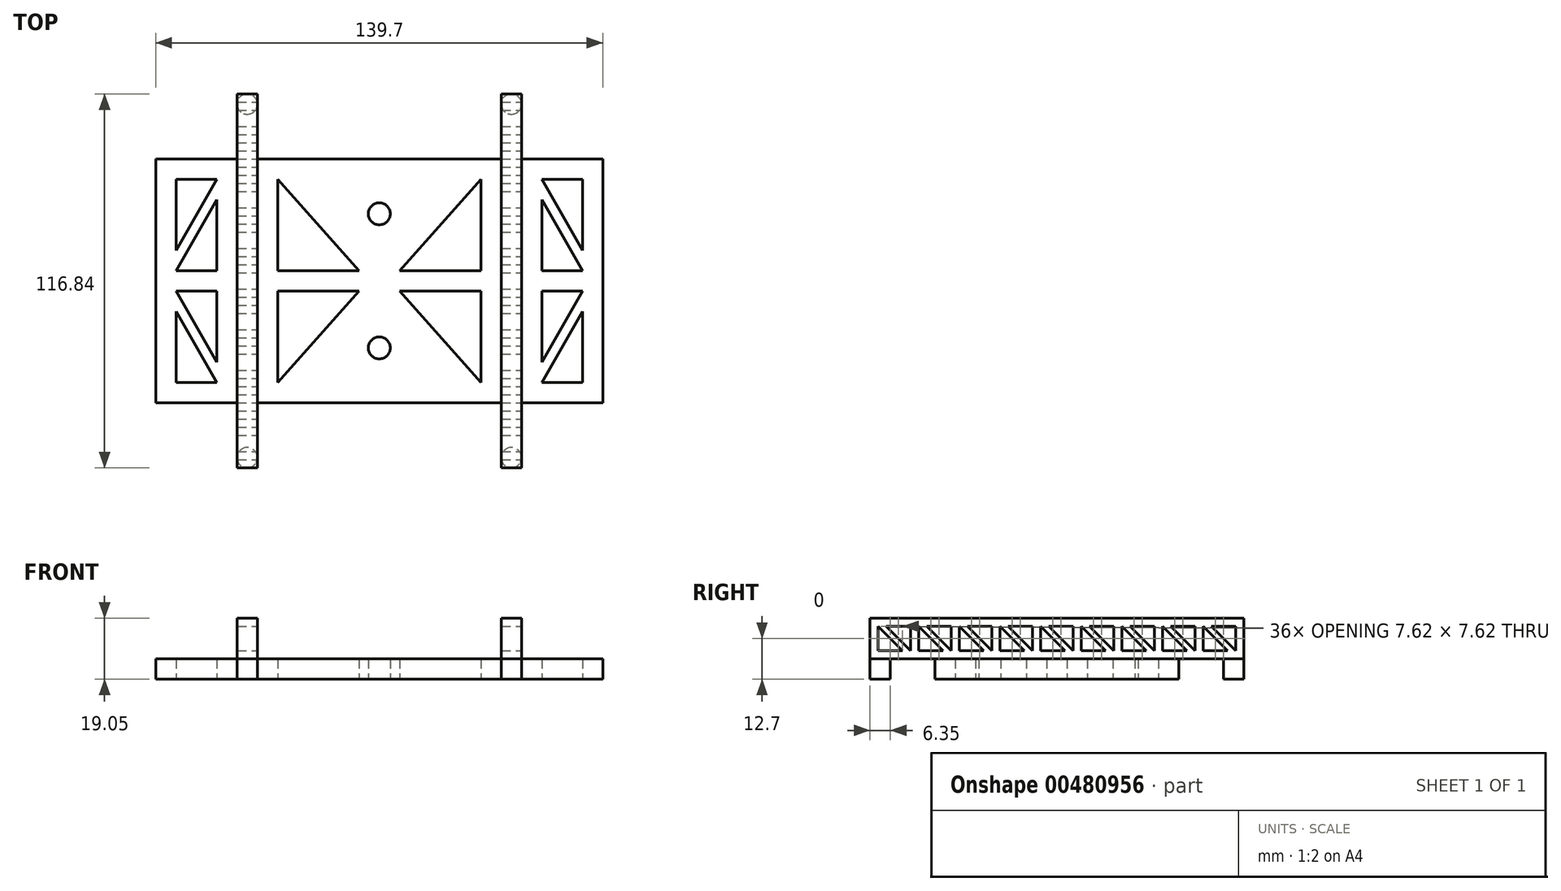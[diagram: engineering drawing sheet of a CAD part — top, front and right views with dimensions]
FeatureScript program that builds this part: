
annotation { "Feature Type Name" : "Feature", "Feature Type Description" : "" }
export const myFeature = defineFeature(function(context is Context, id is Id, definition is map)
    precondition{}
    {
        {
            var Q0;
            Q0=qCreatedBy(makeId("Top.planeOp"),FACE);
            var sketch = newSketch(context, id + "F0", { "sketchPlane" : qUnion([Q0])});
            skLineSegment(sketch, "E0.bottom", {"start": v(-69.85, 38.1) * mm, "end": v(69.85, 38.1) * mm});
            skLineSegment(sketch, "E0.top", {"start": v(-69.85, -38.1) * mm, "end": v(69.85, -38.1) * mm});
            skLineSegment(sketch, "E0.left", {"start": v(-69.85, 38.1) * mm, "end": v(-69.85, -38.1) * mm});
            skLineSegment(sketch, "E0.right", {"start": v(69.85, 38.1) * mm, "end": v(69.85, -38.1) * mm});
            skPoint(sketch, "E0.middle", {"position": v(0, 0) * mm});
            skCircle(sketch, "E1", {"center": v(0, -20.95) * mm, "radius": 3.43 * mm});
            skCircle(sketch, "E2", {"center": v(0, 20.95) * mm, "radius": 3.43 * mm});
            skPoint(sketch, "E2.centerSnap0", {"position": v(0, 38.1) * mm});
            skLineSegment(sketch, "E3", {"start": v(-63.5, 9.52) * mm, "end": v(-63.5, 31.75) * mm});
            skLineSegment(sketch, "E4", {"start": v(-63.5, 31.75) * mm, "end": v(-50.8, 31.75) * mm});
            skLineSegment(sketch, "E5", {"start": v(-50.8, 31.75) * mm, "end": v(-63.5, 9.52) * mm});
            skLineSegment(sketch, "E6", {"start": v(-50.8, 3.17) * mm, "end": v(-50.8, 25.4) * mm});
            skLineSegment(sketch, "E7", {"start": v(-50.8, 25.4) * mm, "end": v(-63.5, 3.17) * mm});
            skLineSegment(sketch, "E8", {"start": v(-63.5, 3.17) * mm, "end": v(-50.8, 3.17) * mm});
            skLineSegment(sketch, "E9.MirrorCS", {"start": v(-63.5, -3.17) * mm, "end": v(-50.8, -3.17) * mm});
            skLineSegment(sketch, "E10.MirrorCS", {"start": v(-50.8, -3.17) * mm, "end": v(-50.8, -25.4) * mm});
            skLineSegment(sketch, "E11.MirrorCS", {"start": v(-50.8, -25.4) * mm, "end": v(-63.5, -3.17) * mm});
            skLineSegment(sketch, "E12.MirrorCS", {"start": v(-50.8, -31.75) * mm, "end": v(-63.5, -9.52) * mm});
            skLineSegment(sketch, "E13.MirrorCS", {"start": v(-63.5, -31.75) * mm, "end": v(-50.8, -31.75) * mm});
            skLineSegment(sketch, "E14.MirrorCS", {"start": v(-63.5, -9.52) * mm, "end": v(-63.5, -31.75) * mm});
            skLineSegment(sketch, "E15.MirrorCS", {"start": v(50.8, 3.17) * mm, "end": v(50.8, 25.4) * mm});
            skLineSegment(sketch, "E16.MirrorCS", {"start": v(50.8, 25.4) * mm, "end": v(63.5, 3.17) * mm});
            skLineSegment(sketch, "E17.MirrorCS", {"start": v(63.5, 3.17) * mm, "end": v(50.8, 3.17) * mm});
            skLineSegment(sketch, "E18.MirrorCS", {"start": v(50.8, 31.75) * mm, "end": v(63.5, 9.52) * mm});
            skLineSegment(sketch, "E19.MirrorCS", {"start": v(63.5, 9.52) * mm, "end": v(63.5, 31.75) * mm});
            skLineSegment(sketch, "E20.MirrorCS", {"start": v(63.5, 31.75) * mm, "end": v(50.8, 31.75) * mm});
            skLineSegment(sketch, "E21.MirrorCS", {"start": v(50.8, -25.4) * mm, "end": v(63.5, -3.17) * mm});
            skLineSegment(sketch, "E22.MirrorCS", {"start": v(63.5, -3.17) * mm, "end": v(50.8, -3.17) * mm});
            skLineSegment(sketch, "E23.MirrorCS", {"start": v(50.8, -3.17) * mm, "end": v(50.8, -25.4) * mm});
            skLineSegment(sketch, "E24.MirrorCS", {"start": v(63.5, -9.52) * mm, "end": v(63.5, -31.75) * mm});
            skLineSegment(sketch, "E25.MirrorCS", {"start": v(50.8, -31.75) * mm, "end": v(63.5, -9.52) * mm});
            skLineSegment(sketch, "E26.MirrorCS", {"start": v(63.5, -31.75) * mm, "end": v(50.8, -31.75) * mm});
            skLineSegment(sketch, "E27", {"start": v(-31.75, 3.17) * mm, "end": v(-31.75, 31.75) * mm});
            skLineSegment(sketch, "E28", {"start": v(-31.75, 31.75) * mm, "end": v(-6.35, 3.17) * mm});
            skLineSegment(sketch, "E29", {"start": v(-6.35, 3.17) * mm, "end": v(-31.75, 3.17) * mm});
            skLineSegment(sketch, "E30", {"start": v(-31.75, -3.17) * mm, "end": v(-31.75, -31.75) * mm});
            skLineSegment(sketch, "E31", {"start": v(-31.75, -31.75) * mm, "end": v(-6.35, -3.17) * mm});
            skLineSegment(sketch, "E32", {"start": v(-6.35, -3.17) * mm, "end": v(-31.75, -3.17) * mm});
            skLineSegment(sketch, "E33.MirrorCS", {"start": v(31.75, 31.75) * mm, "end": v(6.35, 3.17) * mm});
            skLineSegment(sketch, "E34.MirrorCS", {"start": v(31.75, 3.17) * mm, "end": v(31.75, 31.75) * mm});
            skLineSegment(sketch, "E35.MirrorCS", {"start": v(6.35, 3.17) * mm, "end": v(31.75, 3.17) * mm});
            skLineSegment(sketch, "E36.MirrorCS", {"start": v(6.35, -3.17) * mm, "end": v(31.75, -3.17) * mm});
            skLineSegment(sketch, "E37.MirrorCS", {"start": v(31.75, -3.17) * mm, "end": v(31.75, -31.75) * mm});
            skLineSegment(sketch, "E38.MirrorCS", {"start": v(31.75, -31.75) * mm, "end": v(6.35, -3.17) * mm});
            skSolve(sketch);
        }
        {
            var Q0;
            Q0=makeQuery(id+"F0.imprint","IMPRINT",FACE,{"disambiguationData":[TD([[makeQuery(id+"F0.imprint","IMPRINT",EDGE,{"derivedFrom":sQuery(id+"F0.wireOp",EDGE,"E0.bottom")}),-1.0]])]});
            extrude(context, id + "F1", {"entities" : qUnion([Q0]), "depth" : 6.35 * mm});
        }
        {
            var Q0;
            Q0=makeQuery(id+"F1.opExtrude","CAP_FACE",FACE,{"disambiguationData":[OSD([sQuery(id+"F0.wireOp",EDGE,"E0.bottom"),sQuery(id+"F0.wireOp",EDGE,"E0.top"),sQuery(id+"F0.wireOp",EDGE,"E0.left"),sQuery(id+"F0.wireOp",EDGE,"E0.right")])],"isStart":false});
            var sketch = newSketch(context, id + "F2", { "sketchPlane" : qUnion([Q0])});
            skLineSegment(sketch, "E39.bottom", {"start": v(38.1, 58.42) * mm, "end": v(44.45, 58.42) * mm});
            skLineSegment(sketch, "E39.top", {"start": v(38.1, -58.42) * mm, "end": v(44.45, -58.42) * mm});
            skLineSegment(sketch, "E39.left", {"start": v(38.1, 58.42) * mm, "end": v(38.1, -58.42) * mm});
            skLineSegment(sketch, "E39.right", {"start": v(44.45, 58.42) * mm, "end": v(44.45, -58.42) * mm});
            skPoint(sketch, "E39.middle", {"position": v(41.28, 0) * mm});
            skLineSegment(sketch, "E40", {"start": v(0, 55.36) * mm, "end": v(0, -69.96) * mm, "construction": true});
            skLineSegment(sketch, "E41.MirrorCS", {"start": v(-38.1, 58.42) * mm, "end": v(-38.1, -58.42) * mm});
            skLineSegment(sketch, "E42.MirrorCS", {"start": v(-44.45, 58.42) * mm, "end": v(-44.45, -58.42) * mm});
            skLineSegment(sketch, "E43.MirrorCS", {"start": v(-38.1, -58.42) * mm, "end": v(-44.45, -58.42) * mm});
            skLineSegment(sketch, "E44.MirrorCS", {"start": v(-38.1, 58.42) * mm, "end": v(-44.45, 58.42) * mm});
            skSolve(sketch);
        }
        {
            var Q0;
            {var subQ0=sQuery(id+"F2.wireOp",EDGE,"04U5UkVg-AJ8Z-mwcw-HsoT-IvXdQoQTUmTr.bottom");Q0=makeQuery(id+"F2.imprint","IMPRINT",FACE,{"disambiguationData":[TD([[makeQuery(id+"F2.imprint","IMPRINT",EDGE,{"derivedFrom":subQ0}),-1.0]])]});}
            var Q1;
            {var subQ0=sQuery(id+"F2.wireOp",EDGE,"04U5UkVg-AJ8Z-mwcw-HsoT-IvXdQoQTUmTr.left");var subQ1=makeQuery(id+"F1.opExtrude","CAP_EDGE",EDGE,{"disambiguationData":[OSD([sQuery(id+"F0.wireOp",EDGE,"E0.bottom")])],"isStart":false});var subQ2=makeQuery(id+"F2.imprint","INTERSECT",VERTEX,{"derivedFrom":[subQ1,subQ0]});Q1=makeQuery(id+"F2.imprint","IMPRINT",FACE,{"disambiguationData":[TD([[makeQuery(id+"F2.imprint","IMPRINT",EDGE,{"disambiguationData":[TD([[subQ2,-1.0]])],"derivedFrom":subQ0}),1.0]])]});}
            var Q2;
            {var subQ0=sQuery(id+"F2.wireOp",EDGE,"04U5UkVg-AJ8Z-mwcw-HsoT-IvXdQoQTUmTr.top");Q2=makeQuery(id+"F2.imprint","IMPRINT",FACE,{"disambiguationData":[TD([[makeQuery(id+"F2.imprint","IMPRINT",EDGE,{"derivedFrom":subQ0}),1.0]])]});}
            var Q3;
            {var subQ0=sQuery(id+"F2.wireOp",EDGE,"E39.top");Q3=makeQuery(id+"F2.imprint","IMPRINT",FACE,{"disambiguationData":[TD([[makeQuery(id+"F2.imprint","IMPRINT",EDGE,{"derivedFrom":subQ0}),1.0]])]});}
            var Q4;
            {var subQ0=sQuery(id+"F2.wireOp",EDGE,"E39.left");var subQ1=makeQuery(id+"F1.opExtrude","CAP_EDGE",EDGE,{"disambiguationData":[OSD([sQuery(id+"F0.wireOp",EDGE,"E0.bottom")])],"isStart":false});var subQ2=makeQuery(id+"F2.imprint","INTERSECT",VERTEX,{"derivedFrom":[subQ1,subQ0]});Q4=makeQuery(id+"F2.imprint","IMPRINT",FACE,{"disambiguationData":[TD([[makeQuery(id+"F2.imprint","IMPRINT",EDGE,{"disambiguationData":[TD([[subQ2,-1.0]])],"derivedFrom":subQ0}),1.0]])]});}
            var Q5;
            {var subQ0=sQuery(id+"F2.wireOp",EDGE,"E39.bottom");Q5=makeQuery(id+"F2.imprint","IMPRINT",FACE,{"disambiguationData":[TD([[makeQuery(id+"F2.imprint","IMPRINT",EDGE,{"derivedFrom":subQ0}),-1.0]])]});}
            var Q6;
            {var subQ0=sQuery(id+"F2.wireOp",EDGE,"E44.MirrorCS");Q6=makeQuery(id+"F2.imprint","IMPRINT",FACE,{"disambiguationData":[TD([[makeQuery(id+"F2.imprint","IMPRINT",EDGE,{"derivedFrom":subQ0}),1.0]])]});}
            var Q7;
            {var subQ0=sQuery(id+"F2.wireOp",EDGE,"E41.MirrorCS");var subQ1=makeQuery(id+"F1.opExtrude","CAP_EDGE",EDGE,{"disambiguationData":[OSD([sQuery(id+"F0.wireOp",EDGE,"E0.bottom")])],"isStart":false});var subQ2=makeQuery(id+"F2.imprint","INTERSECT",VERTEX,{"derivedFrom":[subQ1,subQ0]});Q7=makeQuery(id+"F2.imprint","IMPRINT",FACE,{"disambiguationData":[TD([[makeQuery(id+"F2.imprint","IMPRINT",EDGE,{"disambiguationData":[TD([[subQ2,-1.0]])],"derivedFrom":subQ0}),-1.0]])]});}
            var Q8;
            {var subQ0=sQuery(id+"F2.wireOp",EDGE,"E43.MirrorCS");Q8=makeQuery(id+"F2.imprint","IMPRINT",FACE,{"disambiguationData":[TD([[makeQuery(id+"F2.imprint","IMPRINT",EDGE,{"derivedFrom":subQ0}),-1.0]])]});}
            extrude(context, id + "F3", {"entities" : qUnion([Q0, Q1, Q2, Q3, Q4, Q5, Q6, Q7, Q8]), "operationType" : NewBodyOperationType.ADD, "depth" : 12.7 * mm});
        }
        {
            var Q0;
            Q0=makeQuery(id+"F3.opExtrude","SWEPT_FACE",FACE,{"disambiguationData":[OSD([sQuery(id+"F2.wireOp",EDGE,"E39.right")])]});
            var sketch = newSketch(context, id + "F4", { "sketchPlane" : qUnion([Q0])});
            skLineSegment(sketch, "E45", {"start": v(-55.88, 16.51) * mm, "end": v(-55.88, 8.9) * mm});
            skLineSegment(sketch, "E46", {"start": v(-55.88, 8.9) * mm, "end": v(-48.26, 8.9) * mm});
            skLineSegment(sketch, "E47", {"start": v(-48.26, 8.9) * mm, "end": v(-55.88, 16.51) * mm});
            skLineSegment(sketch, "E48", {"start": v(-53.34, 16.51) * mm, "end": v(-45.72, 8.9) * mm});
            skLineSegment(sketch, "E49", {"start": v(-45.72, 8.9) * mm, "end": v(-45.72, 16.51) * mm});
            skLineSegment(sketch, "E50", {"start": v(-45.72, 16.51) * mm, "end": v(-53.34, 16.51) * mm});
            skLineSegment(sketch, "E51.1.0.0", {"start": v(-33.02, 8.89) * mm, "end": v(-33.02, 16.51) * mm});
            skLineSegment(sketch, "E51.1.0.1", {"start": v(-40.64, 16.51) * mm, "end": v(-33.02, 8.9) * mm});
            skLineSegment(sketch, "E51.1.0.2", {"start": v(-33.02, 16.51) * mm, "end": v(-40.64, 16.51) * mm});
            skLineSegment(sketch, "E51.1.0.3", {"start": v(-35.56, 8.9) * mm, "end": v(-43.18, 16.51) * mm});
            skLineSegment(sketch, "E51.1.0.4", {"start": v(-43.18, 16.5) * mm, "end": v(-43.18, 8.9) * mm});
            skLineSegment(sketch, "E51.1.0.5", {"start": v(-43.18, 8.9) * mm, "end": v(-35.56, 8.9) * mm});
            skLineSegment(sketch, "E51.2.0.0", {"start": v(-20.32, 8.89) * mm, "end": v(-20.32, 16.51) * mm});
            skLineSegment(sketch, "E51.2.0.1", {"start": v(-27.94, 16.51) * mm, "end": v(-20.32, 8.9) * mm});
            skLineSegment(sketch, "E51.2.0.2", {"start": v(-20.32, 16.51) * mm, "end": v(-27.94, 16.51) * mm});
            skLineSegment(sketch, "E51.2.0.3", {"start": v(-22.86, 8.89) * mm, "end": v(-30.48, 16.5) * mm});
            skLineSegment(sketch, "E51.2.0.4", {"start": v(-30.48, 16.5) * mm, "end": v(-30.48, 8.89) * mm});
            skLineSegment(sketch, "E51.2.0.5", {"start": v(-30.48, 8.9) * mm, "end": v(-22.86, 8.9) * mm});
            skLineSegment(sketch, "E51.3.0.0", {"start": v(-7.62, 8.89) * mm, "end": v(-7.62, 16.5) * mm});
            skLineSegment(sketch, "E51.3.0.1", {"start": v(-15.24, 16.51) * mm, "end": v(-7.62, 8.89) * mm});
            skLineSegment(sketch, "E51.3.0.2", {"start": v(-7.62, 16.51) * mm, "end": v(-15.24, 16.51) * mm});
            skLineSegment(sketch, "E51.3.0.3", {"start": v(-10.16, 8.9) * mm, "end": v(-17.78, 16.51) * mm});
            skLineSegment(sketch, "E51.3.0.4", {"start": v(-17.78, 16.5) * mm, "end": v(-17.78, 8.89) * mm});
            skLineSegment(sketch, "E51.3.0.5", {"start": v(-17.78, 8.9) * mm, "end": v(-10.16, 8.9) * mm});
            skLineSegment(sketch, "E51.4.0.0", {"start": v(5.08, 8.89) * mm, "end": v(5.08, 16.5) * mm});
            skLineSegment(sketch, "E51.4.0.1", {"start": v(-2.54, 16.51) * mm, "end": v(5.08, 8.89) * mm});
            skLineSegment(sketch, "E51.4.0.2", {"start": v(5.08, 16.51) * mm, "end": v(-2.54, 16.51) * mm});
            skLineSegment(sketch, "E51.4.0.3", {"start": v(2.54, 8.89) * mm, "end": v(-5.08, 16.5) * mm});
            skLineSegment(sketch, "E51.4.0.4", {"start": v(-5.08, 16.5) * mm, "end": v(-5.08, 8.89) * mm});
            skLineSegment(sketch, "E51.4.0.5", {"start": v(-5.08, 8.9) * mm, "end": v(2.54, 8.9) * mm});
            skLineSegment(sketch, "E51.5.0.0", {"start": v(17.78, 8.89) * mm, "end": v(17.78, 16.5) * mm});
            skLineSegment(sketch, "E51.5.0.1", {"start": v(10.16, 16.51) * mm, "end": v(17.78, 8.89) * mm});
            skLineSegment(sketch, "E51.5.0.2", {"start": v(17.78, 16.51) * mm, "end": v(10.16, 16.51) * mm});
            skLineSegment(sketch, "E51.5.0.3", {"start": v(15.24, 8.89) * mm, "end": v(7.62, 16.5) * mm});
            skLineSegment(sketch, "E51.5.0.4", {"start": v(7.62, 16.5) * mm, "end": v(7.62, 8.89) * mm});
            skLineSegment(sketch, "E51.5.0.5", {"start": v(7.62, 8.9) * mm, "end": v(15.24, 8.9) * mm});
            skLineSegment(sketch, "E51.6.0.0", {"start": v(30.48, 8.89) * mm, "end": v(30.48, 16.5) * mm});
            skLineSegment(sketch, "E51.6.0.1", {"start": v(22.86, 16.51) * mm, "end": v(30.48, 8.89) * mm});
            skLineSegment(sketch, "E51.6.0.2", {"start": v(30.48, 16.51) * mm, "end": v(22.86, 16.51) * mm});
            skLineSegment(sketch, "E51.6.0.3", {"start": v(27.94, 8.89) * mm, "end": v(20.32, 16.5) * mm});
            skLineSegment(sketch, "E51.6.0.4", {"start": v(20.32, 16.5) * mm, "end": v(20.32, 8.89) * mm});
            skLineSegment(sketch, "E51.6.0.5", {"start": v(20.32, 8.9) * mm, "end": v(27.94, 8.9) * mm});
            skLineSegment(sketch, "E51.7.0.0", {"start": v(43.18, 8.89) * mm, "end": v(43.18, 16.5) * mm});
            skLineSegment(sketch, "E51.7.0.1", {"start": v(35.56, 16.51) * mm, "end": v(43.18, 8.89) * mm});
            skLineSegment(sketch, "E51.7.0.2", {"start": v(43.18, 16.51) * mm, "end": v(35.56, 16.51) * mm});
            skLineSegment(sketch, "E51.7.0.3", {"start": v(40.64, 8.89) * mm, "end": v(33.02, 16.5) * mm});
            skLineSegment(sketch, "E51.7.0.4", {"start": v(33.02, 16.5) * mm, "end": v(33.02, 8.89) * mm});
            skLineSegment(sketch, "E51.7.0.5", {"start": v(33.02, 8.9) * mm, "end": v(40.64, 8.9) * mm});
            skLineSegment(sketch, "E51.8.0.0", {"start": v(55.88, 8.89) * mm, "end": v(55.88, 16.5) * mm});
            skLineSegment(sketch, "E51.8.0.1", {"start": v(48.26, 16.51) * mm, "end": v(55.88, 8.89) * mm});
            skLineSegment(sketch, "E51.8.0.2", {"start": v(55.88, 16.51) * mm, "end": v(48.26, 16.51) * mm});
            skLineSegment(sketch, "E51.8.0.3", {"start": v(53.34, 8.89) * mm, "end": v(45.72, 16.5) * mm});
            skLineSegment(sketch, "E51.8.0.4", {"start": v(45.72, 16.5) * mm, "end": v(45.72, 8.89) * mm});
            skLineSegment(sketch, "E51.8.0.5", {"start": v(45.72, 8.9) * mm, "end": v(53.34, 8.9) * mm});
            skLineSegment(sketch, "E51.direction1", {"start": v(-45.72, 8.9) * mm, "end": v(-33.02, 8.9) * mm, "construction": true});
            skSolve(sketch);
        }
        {
            var Q0;
            Q0=qSketchRegion(id+"F4",true);
            extrude(context, id + "F5", {"entities" : qUnion([Q0]), "operationType" : NewBodyOperationType.REMOVE, "endBound" : BoundingType.THROUGH_ALL, "oppositeDirection" : true, "depth" : 6.35 * mm});
        }
        {
            var Q0;
            {var subQ0=sQuery(id+"F2.wireOp",EDGE,"E41.MirrorCS");var subQ1=sQuery(id+"F0.wireOp",EDGE,"E0.top");var subQ2=sQuery(id+"F2.wireOp",EDGE,"E42.MirrorCS");var subQ3=sQuery(id+"F2.wireOp",EDGE,"E43.MirrorCS");Q0=makeQuery(id+"F3.boolean.opBoolean","SPLIT",FACE,{"disambiguationData":[TD([makeQuery(id+"F1.opExtrude","SWEPT_FACE",FACE,{"disambiguationData":[OSD([subQ1])]})])],"derivedFrom":makeQuery(id+"F3.opExtrude","CAP_FACE",FACE,{"disambiguationData":[OSD([subQ0,subQ2,subQ3,sQuery(id+"F2.wireOp",EDGE,"E44.MirrorCS")])],"isStart":true})});}
            var sketch = newSketch(context, id + "F6", { "sketchPlane" : qUnion([Q0])});
            skCircle(sketch, "E52", {"center": v(-41.28, 55.24) * mm, "radius": 3.18 * mm});
            skCircle(sketch, "E53", {"center": v(41.28, 55.24) * mm, "radius": 3.18 * mm});
            skCircle(sketch, "E54", {"center": v(-41.28, -55.24) * mm, "radius": 3.18 * mm});
            skCircle(sketch, "E55", {"center": v(41.28, -55.24) * mm, "radius": 3.18 * mm});
            skSolve(sketch);
        }
        {
            var Q0;
            {var subQ0=sQuery(id+"F6.wireOp",EDGE,"E52");var subQ1=sQuery(id+"F2.wireOp",EDGE,"E43.MirrorCS");var subQ2=makeQuery(id+"F6.imprint","INTERSECT",VERTEX,{"derivedFrom":[makeQuery(id+"F3.opExtrude","CAP_EDGE",EDGE,{"disambiguationData":[OSD([subQ1])],"isStart":true}),subQ0]});Q0=makeQuery(id+"F6.imprint","IMPRINT",FACE,{"disambiguationData":[TD([[makeQuery(id+"F6.imprint","IMPRINT",EDGE,{"disambiguationData":[TD([[subQ2,1.0]])],"derivedFrom":subQ0}),1.0]])]});}
            var Q1;
            Q1=makeQuery(id+"F6.imprint","IMPRINT",FACE,{"disambiguationData":[TD([[makeQuery(id+"F6.imprint","IMPRINT",EDGE,{"derivedFrom":sQuery(id+"F6.wireOp",EDGE,"E53")}),1.0]])]});
            var Q2;
            Q2=makeQuery(id+"F6.imprint","IMPRINT",FACE,{"disambiguationData":[TD([[makeQuery(id+"F6.imprint","IMPRINT",EDGE,{"derivedFrom":sQuery(id+"F6.wireOp",EDGE,"E54")}),1.0]])]});
            var Q3;
            Q3=makeQuery(id+"F6.imprint","IMPRINT",FACE,{"disambiguationData":[TD([[makeQuery(id+"F6.imprint","IMPRINT",EDGE,{"derivedFrom":sQuery(id+"F6.wireOp",EDGE,"E55")}),1.0]])]});
            extrude(context, id + "F7", {"entities" : qUnion([Q0, Q1, Q2, Q3]), "operationType" : NewBodyOperationType.ADD, "depth" : 6.35 * mm});
        }
    });
